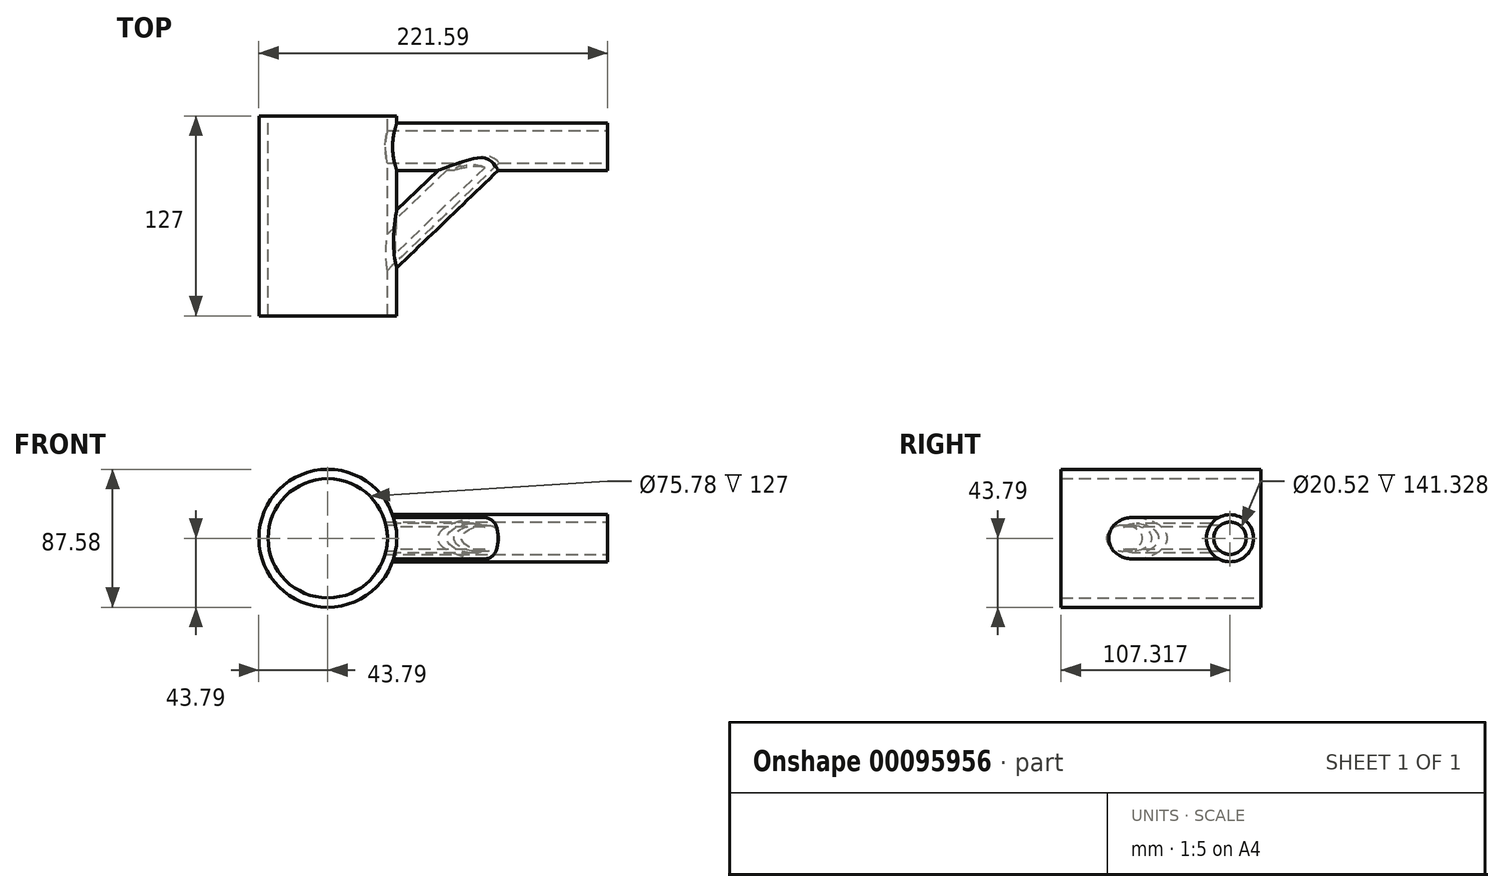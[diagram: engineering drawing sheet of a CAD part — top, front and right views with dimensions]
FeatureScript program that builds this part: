
annotation { "Feature Type Name" : "Feature", "Feature Type Description" : "" }
export const myFeature = defineFeature(function(context is Context, id is Id, definition is map)
    precondition{}
    {
        {
            var Q0;
            Q0=qCreatedBy(makeId("Front.planeOp"),FACE);
            var sketch = newSketch(context, id + "F0", { "sketchPlane" : qUnion([Q0])});
            skCircle(sketch, "E0", {"center": v(0, 0) * mm, "radius": 43.79 * mm});
            skSolve(sketch);
        }
        {
            var Q0;
            Q0 = qSketchRegion(id + "F0", true);
            extrude(context, id + "F1", {"entities" : qUnion([Q0]), "endBound" : BoundingType.SYMMETRIC, "depth" : 127 * mm});
        }
        {
            var Q0;
            Q0=makeQuery(id+"F1.opExtrude","CAP_FACE",FACE,{"disambiguationData":[OSD([sQuery(id+"F0.wireOp",EDGE,"E0")])],"isStart":false});
            var sketch = newSketch(context, id + "F2", { "sketchPlane" : qUnion([Q0])});
            skCircle(sketch, "E1", {"center": v(0, 0) * mm, "radius": 36.95 * mm});
            skSolve(sketch);
        }
        {
            var Q0;
            Q0 = qSketchRegion(id + "F2", true);
            extrude(context, id + "F3", {"entities" : qUnion([Q0]), "operationType" : NewBodyOperationType.REMOVE, "endBound" : BoundingType.THROUGH_ALL, "oppositeDirection" : true, "depth" : 25.4 * mm});
        }
        {
            var Q0;
            Q0=qCreatedBy(makeId("Right.planeOp"),FACE);
            var sketch = newSketch(context, id + "F4", { "sketchPlane" : qUnion([Q0])});
            skCircle(sketch, "E2", {"center": v(43.82, 0) * mm, "radius": 14.96 * mm});
            skSolve(sketch);
        }
        {
            var Q0;
            Q0 = qSketchRegion(id + "F4", true);
            extrude(context, id + "F5", {"entities" : qUnion([Q0]), "operationType" : NewBodyOperationType.ADD, "depth" : 177.8 * mm});
        }
        {
            var Q0;
            Q0=makeQuery(id+"F5.opExtrude","CAP_FACE",FACE,{"disambiguationData":[OSD([sQuery(id+"F4.wireOp",EDGE,"E2")])],"isStart":false});
            var sketch = newSketch(context, id + "F6", { "sketchPlane" : qUnion([Q0])});
            skCircle(sketch, "E3", {"center": v(43.82, 0) * mm, "radius": 10.23 * mm});
            skSolve(sketch);
        }
        {
            var Q0;
            Q0 = qSketchRegion(id + "F6", true);
            extrude(context, id + "F7", {"entities" : qUnion([Q0]), "operationType" : NewBodyOperationType.REMOVE, "oppositeDirection" : true, "depth" : 177.8 * mm});
        }
        {
            var Q0;
            Q0 = qSketchRegion(id + "F2", true);
            extrude(context, id + "F8", {"entities" : qUnion([Q0]), "operationType" : NewBodyOperationType.REMOVE, "endBound" : BoundingType.THROUGH_ALL, "oppositeDirection" : true, "depth" : 25.4 * mm});
        }
        {
            var Q0;
            Q0=qCreatedBy(makeId("Top.planeOp"),FACE);
            var sketch = newSketch(context, id + "F9", { "sketchPlane" : qUnion([Q0])});
            skLineSegment(sketch, "E4", {"start": v(4.98, -18.24) * mm, "end": v(37.24, -51.78) * mm});
            skLineSegment(sketch, "E5", {"start": v(37.24, -51.78) * mm, "end": v(30.22, -58.53) * mm});
            skLineSegment(sketch, "E6", {"start": v(30.22, -58.53) * mm, "end": v(-1.82, -25.22) * mm});
            skLineSegment(sketch, "E7", {"start": v(-1.82, -25.22) * mm, "end": v(4.98, -18.24) * mm});
            skSolve(sketch);
        }
        {
            var Q0;
            Q0 = qSketchRegion(id + "F9", true);
            extrude(context, id + "F10", {"entities" : qUnion([Q0]), "operationType" : NewBodyOperationType.ADD, "endBound" : BoundingType.SYMMETRIC, "depth" : 43.6 * mm});
        }
        {
            var Q0;
            Q0=makeQuery(id+"F10.opExtrude","SWEPT_FACE",FACE,{"disambiguationData":[OSD([sQuery(id+"F9.wireOp",EDGE,"E6")])]});
            var sketch = newSketch(context, id + "F11", { "sketchPlane" : qUnion([Q0])});
            skCircle(sketch, "E8", {"center": v(40.94, 0) * mm, "radius": 13.28 * mm});
            skCircle(sketch, "E9", {"center": v(40.94, 0) * mm, "radius": 9.41 * mm});
            skSolve(sketch);
        }
        {
            var Q0;
            Q0 = qSketchRegion(id + "F11", true);
            extrude(context, id + "F12", {"entities" : qUnion([Q0]), "operationType" : NewBodyOperationType.ADD, "oppositeDirection" : true, "depth" : 119.07 * mm});
        }
        {
            var Q0;
            Q0=makeQuery(id+"F10.opExtrude","SWEPT_FACE",FACE,{"disambiguationData":[OSD([sQuery(id+"F9.wireOp",EDGE,"E6")])]});
            var sketch = newSketch(context, id + "F13", { "sketchPlane" : qUnion([Q0])});
            skCircle(sketch, "E10", {"center": v(42.96, 0) * mm, "radius": 8.24 * mm});
            skSolve(sketch);
        }
        {
            var Q0;
            Q0 = qSketchRegion(id + "F13", true);
            extrude(context, id + "F14", {"entities" : qUnion([Q0]), "operationType" : NewBodyOperationType.REMOVE, "oppositeDirection" : true, "depth" : 126.55 * mm});
        }
        {
            var Q0;
            Q0=qCreatedBy(makeId("Front.planeOp"),FACE);
            var sketch = newSketch(context, id + "F15", { "sketchPlane" : qUnion([Q0])});
            skCircle(sketch, "E11", {"center": v(0, 0) * mm, "radius": 37.9 * mm});
            skSolve(sketch);
        }
        {
            var Q0;
            Q0 = qSketchRegion(id + "F15", true);
            extrude(context, id + "F16", {"entities" : qUnion([Q0]), "operationType" : NewBodyOperationType.REMOVE, "endBound" : BoundingType.THROUGH_ALL, "depth" : 104.51 * mm});
        }
        {
            var Q0;
            Q0=makeQuery(id+"F5.opExtrude","CAP_FACE",FACE,{"disambiguationData":[OSD([sQuery(id+"F4.wireOp",EDGE,"E2")])],"isStart":false});
            var sketch = newSketch(context, id + "F17", { "sketchPlane" : qUnion([Q0])});
            skCircle(sketch, "E12", {"center": v(43.82, 0) * mm, "radius": 10.26 * mm});
            skSolve(sketch);
        }
        {
            var Q0;
            Q0 = qSketchRegion(id + "F17", true);
            extrude(context, id + "F18", {"entities" : qUnion([Q0]), "operationType" : NewBodyOperationType.REMOVE, "oppositeDirection" : true, "depth" : 185.08 * mm});
        }
        {
            var Q0;
            Q0 = qSketchRegion(id + "F15", true);
            extrude(context, id + "F19", {"entities" : qUnion([Q0]), "operationType" : NewBodyOperationType.REMOVE, "oppositeDirection" : true, "depth" : 161.76 * mm});
        }
    });
